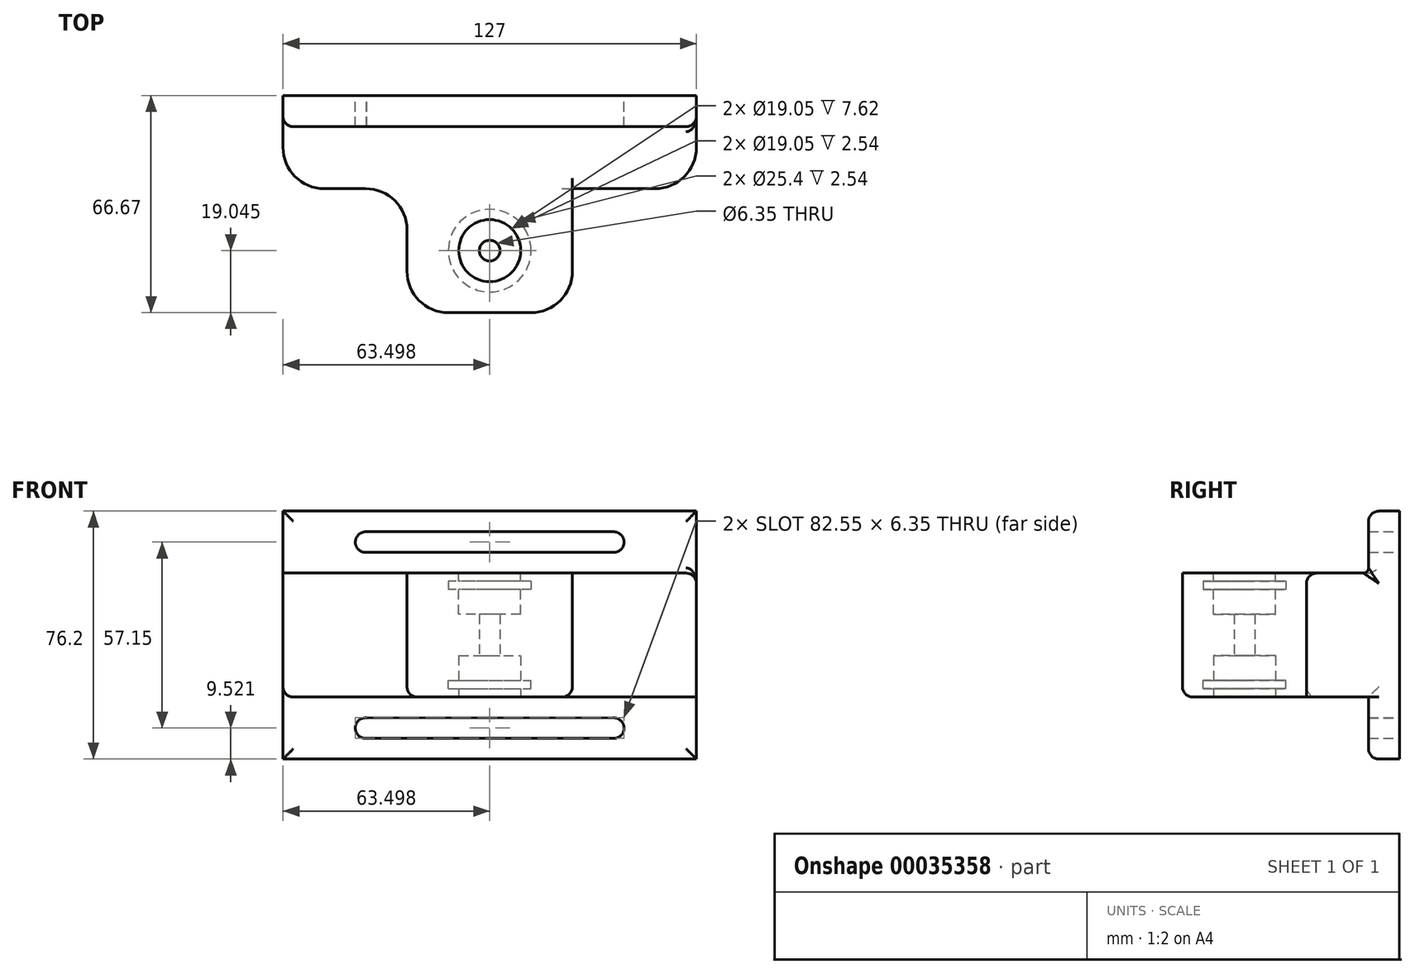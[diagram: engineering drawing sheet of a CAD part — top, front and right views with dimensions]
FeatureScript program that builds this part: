
annotation { "Feature Type Name" : "Feature", "Feature Type Description" : "" }
export const myFeature = defineFeature(function(context is Context, id is Id, definition is map)
    precondition{}
    {
        {
            var Q0;
            Q0=qCreatedBy(makeId("Front.planeOp"),FACE);
            var sketch = newSketch(context, id + "F0", { "sketchPlane" : qUnion([Q0])});
            skLineSegment(sketch, "E0.bottom", {"start": v(-70.41, 43.13) * mm, "end": v(56.59, 43.13) * mm});
            skLineSegment(sketch, "E0.top", {"start": v(-70.41, -33.07) * mm, "end": v(56.59, -33.07) * mm});
            skLineSegment(sketch, "E0.left", {"start": v(-70.41, 43.13) * mm, "end": v(-70.41, -33.07) * mm});
            skLineSegment(sketch, "E0.right", {"start": v(56.59, 43.13) * mm, "end": v(56.59, -33.07) * mm});
            skArc(sketch, "E1", {"start": v(-44.67, -20.4) * mm, "mid": v(-48.19, -23.48) * mm, "end": v(-44.8, -26.72) * mm});
            skArc(sketch, "E2", {"start": v(31.19, -26.72) * mm, "mid": v(34.36, -23.55) * mm, "end": v(31.19, -20.37) * mm});
            skLineSegment(sketch, "E3", {"start": v(-45.36, -20.4) * mm, "end": v(31.19, -20.37) * mm});
            skLineSegment(sketch, "E4", {"start": v(-45.23, -26.72) * mm, "end": v(31.19, -26.72) * mm});
            skLineSegment(sketch, "E5", {"start": v(-70.41, 5.03) * mm, "end": v(56.59, 5.03) * mm, "construction": true});
            skLineSegment(sketch, "E6.MirrorCS", {"start": v(-45.36, 30.44) * mm, "end": v(31.19, 30.43) * mm});
            skLineSegment(sketch, "E7.MirrorCS", {"start": v(-45.23, 36.77) * mm, "end": v(31.19, 36.78) * mm});
            skArc(sketch, "E8.MirrorCS", {"start": v(31.19, 36.78) * mm, "mid": v(34.36, 33.6) * mm, "end": v(31.19, 30.43) * mm});
            skArc(sketch, "E9.MirrorCS", {"start": v(-44.67, 30.44) * mm, "mid": v(-48.19, 33.53) * mm, "end": v(-44.8, 36.77) * mm});
            skSolve(sketch);
        }
        {
            var Q0;
            Q0=makeQuery(id+"F0.imprint","IMPRINT",FACE,{"disambiguationData":[TD([[makeQuery(id+"F0.imprint","IMPRINT",EDGE,{"derivedFrom":sQuery(id+"F0.wireOp",EDGE,"E0.bottom")}),-1.0]])]});
            extrude(context, id + "F1", {"entities" : qUnion([Q0]), "depth" : 9.52 * mm});
        }
        {
            var Q0;
            Q0=makeQuery(id+"F1.opExtrude","CAP_FACE",FACE,{"disambiguationData":[OSD([sQuery(id+"F0.wireOp",EDGE,"E0.bottom"),sQuery(id+"F0.wireOp",EDGE,"E0.top"),sQuery(id+"F0.wireOp",EDGE,"E0.left"),sQuery(id+"F0.wireOp",EDGE,"E0.right"),sQuery(id+"F0.wireOp",EDGE,"E1"),sQuery(id+"F0.wireOp",EDGE,"E2"),sQuery(id+"F0.wireOp",EDGE,"E3"),sQuery(id+"F0.wireOp",EDGE,"E4"),sQuery(id+"F0.wireOp",EDGE,"E6.MirrorCS"),sQuery(id+"F0.wireOp",EDGE,"E7.MirrorCS"),sQuery(id+"F0.wireOp",EDGE,"E8.MirrorCS"),sQuery(id+"F0.wireOp",EDGE,"E9.MirrorCS")])],"isStart":false});
            var sketch = newSketch(context, id + "F2", { "sketchPlane" : qUnion([Q0])});
            skLineSegment(sketch, "E10.bottom", {"start": v(-70.41, -14.02) * mm, "end": v(56.59, -14.02) * mm});
            skLineSegment(sketch, "E10.top", {"start": v(-70.41, 24.08) * mm, "end": v(56.59, 24.08) * mm});
            skLineSegment(sketch, "E10.left", {"start": v(-70.41, -14.02) * mm, "end": v(-70.41, 24.08) * mm});
            skLineSegment(sketch, "E10.right", {"start": v(56.59, -14.02) * mm, "end": v(56.59, 24.08) * mm});
            skSolve(sketch);
        }
        {
            var Q0;
            Q0=makeQuery(id+"F2.imprint","IMPRINT",FACE,{"disambiguationData":[TD([[makeQuery(id+"F2.imprint","IMPRINT",EDGE,{"derivedFrom":sQuery(id+"F2.wireOp",EDGE,"E10.bottom")}),1.0]])]});
            extrude(context, id + "F3", {"entities" : qUnion([Q0]), "operationType" : NewBodyOperationType.ADD, "depth" : 19.05 * mm});
        }
        {
            var Q0;
            Q0=makeQuery(id+"F3.opExtrude","CAP_FACE",FACE,{"disambiguationData":[OSD([sQuery(id+"F2.wireOp",EDGE,"E10.bottom"),sQuery(id+"F2.wireOp",EDGE,"E10.top"),sQuery(id+"F2.wireOp",EDGE,"E10.left"),sQuery(id+"F2.wireOp",EDGE,"E10.right")])],"isStart":false});
            var sketch = newSketch(context, id + "F4", { "sketchPlane" : qUnion([Q0])});
            skLineSegment(sketch, "E11.bottom", {"start": v(-32.31, -14.02) * mm, "end": v(18.49, -14.02) * mm});
            skLineSegment(sketch, "E11.top", {"start": v(-32.31, 24.08) * mm, "end": v(18.49, 24.08) * mm});
            skLineSegment(sketch, "E11.left", {"start": v(-32.31, -14.02) * mm, "end": v(-32.31, 24.08) * mm});
            skLineSegment(sketch, "E11.right", {"start": v(18.49, -14.02) * mm, "end": v(18.49, 24.08) * mm});
            skSolve(sketch);
        }
        {
            var Q0;
            Q0=makeQuery(id+"F4.imprint","IMPRINT",FACE,{"disambiguationData":[TD([[makeQuery(id+"F4.imprint","IMPRINT",EDGE,{"derivedFrom":sQuery(id+"F4.wireOp",EDGE,"E11.bottom")}),1.0]])]});
            extrude(context, id + "F5", {"entities" : qUnion([Q0]), "operationType" : NewBodyOperationType.ADD, "depth" : 38.1 * mm});
        }
        {
            var Q0;
            Q0=makeQuery(id+"F5.boolean.opBoolean","MERGE",FACE,{"derivedFrom":[makeQuery(id+"F3.opExtrude","SWEPT_FACE",FACE,{"disambiguationData":[OSD([sQuery(id+"F2.wireOp",EDGE,"E10.bottom")])]}),makeQuery(id+"F5.opExtrude","SWEPT_FACE",FACE,{"disambiguationData":[OSD([sQuery(id+"F4.wireOp",EDGE,"E11.bottom")])]})]});
            var sketch = newSketch(context, id + "F6", { "sketchPlane" : qUnion([Q0])});
            skPoint(sketch, "E12", {"position": v(-6.91, 47.63) * mm});
            skSolve(sketch);
        }
        {
            var Q0;
            Q0=sQuery(id+"F6.wireOp",VERTEX,"E12");
            var Q1;
            Q1=makeQuery(id+"F1.opExtrude","SWEPT_BODY",BODY,{"disambiguationData":[OSD([sQuery(id+"F0.wireOp",EDGE,"E0.bottom"),sQuery(id+"F0.wireOp",EDGE,"E0.top"),sQuery(id+"F0.wireOp",EDGE,"E0.left"),sQuery(id+"F0.wireOp",EDGE,"E0.right"),sQuery(id+"F0.wireOp",EDGE,"E1"),sQuery(id+"F0.wireOp",EDGE,"E2"),sQuery(id+"F0.wireOp",EDGE,"E3"),sQuery(id+"F0.wireOp",EDGE,"E4"),sQuery(id+"F0.wireOp",EDGE,"E6.MirrorCS"),sQuery(id+"F0.wireOp",EDGE,"E7.MirrorCS"),sQuery(id+"F0.wireOp",EDGE,"E8.MirrorCS"),sQuery(id+"F0.wireOp",EDGE,"E9.MirrorCS")])]});
            hole(context, id + "F7", {"style" : HoleStyle.C_BORE, "holeDiameter" : 6.35 * mm, "cBoreDiameter" : 19.05 * mm, "cBoreDepth" : 12.7 * mm, "endStyle" : HoleEndStyle.THROUGH, "locations" : qUnion([Q0]), "scope" : qUnion([Q1])});
        }
        {
            var Q0;
            Q0=makeQuery(id+"F5.boolean.opBoolean","MERGE",FACE,{"derivedFrom":[makeQuery(id+"F3.opExtrude","SWEPT_FACE",FACE,{"disambiguationData":[OSD([sQuery(id+"F2.wireOp",EDGE,"E10.top")])]}),makeQuery(id+"F5.opExtrude","SWEPT_FACE",FACE,{"disambiguationData":[OSD([sQuery(id+"F4.wireOp",EDGE,"E11.top")])]})]});
            var sketch = newSketch(context, id + "F8", { "sketchPlane" : qUnion([Q0])});
            skCircle(sketch, "E13.0.0", {"center": v(-6.91, -47.63) * mm, "radius": 9.52 * mm});
            skSolve(sketch);
        }
        {
            var Q0;
            Q0=makeQuery(id+"F8.imprint","IMPRINT",FACE,{"disambiguationData":[TD([[makeQuery(id+"F8.imprint","IMPRINT",EDGE,{"derivedFrom":sQuery(id+"F8.wireOp",EDGE,"E13.0.0")}),1.0]])]});
            extrude(context, id + "F9", {"entities" : qUnion([Q0]), "operationType" : NewBodyOperationType.REMOVE, "oppositeDirection" : true, "depth" : 12.7 * mm});
        }
        {
            var Q0;
            Q0=makeQuery(id+"F5.opExtrude","CAP_EDGE",EDGE,{"disambiguationData":[OSD([sQuery(id+"F4.wireOp",EDGE,"E11.right")])],"isStart":false});
            var Q1;
            Q1=makeQuery(id+"F5.opExtrude","CAP_EDGE",EDGE,{"disambiguationData":[OSD([sQuery(id+"F4.wireOp",EDGE,"E11.left")])],"isStart":false});
            var Q2;
            Q2=makeQuery(id+"F3.opExtrude","CAP_EDGE",EDGE,{"disambiguationData":[OSD([sQuery(id+"F2.wireOp",EDGE,"E10.left")])],"isStart":false});
            var Q3;
            Q3=makeQuery(id+"F5.opExtrude","CAP_EDGE",EDGE,{"disambiguationData":[OSD([sQuery(id+"F4.wireOp",EDGE,"E11.left")])],"isStart":true});
            var Q4;
            Q4=makeQuery(id+"F5.opExtrude","CAP_EDGE",EDGE,{"disambiguationData":[OSD([sQuery(id+"F4.wireOp",EDGE,"E11.right")])],"isStart":true});
            var Q5;
            Q5=makeQuery(id+"F3.opExtrude","CAP_EDGE",EDGE,{"disambiguationData":[OSD([sQuery(id+"F2.wireOp",EDGE,"E10.right")])],"isStart":false});
            fillet(context, id + "F10", {"entities" : qUnion([Q0, Q1, Q2, Q3, Q4, Q5]), "radius" : 12.7 * mm, "tangentPropagation" : true, "allowEdgeOverflow" : false});
        }
        {
            var Q0;
            Q0=makeQuery(id+"F1.opExtrude","SWEPT_FACE",FACE,{"disambiguationData":[OSD([sQuery(id+"F0.wireOp",EDGE,"E0.top")])]});
            cPlane(context, id + "F11", {"entities" : qUnion([Q0]), "cplaneType" : CPlaneType.OFFSET, "offset" : 24.13 * mm, "oppositeDirection" : true, "width" : 152.4 * mm, "height" : 152.4 * mm});
        }
        {
            var Q0;
            Q0=qCreatedBy(id+"F11.planeOp",FACE);
            var sketch = newSketch(context, id + "F12", { "sketchPlane" : qUnion([Q0])});
            skCircle(sketch, "E14", {"center": v(-6.91, 47.63) * mm, "radius": 12.7 * mm});
            skSolve(sketch);
        }
        {
            var Q0;
            Q0=makeQuery(id+"F1.opExtrude","SWEPT_FACE",FACE,{"disambiguationData":[OSD([sQuery(id+"F0.wireOp",EDGE,"E0.bottom")])]});
            cPlane(context, id + "F13", {"entities" : qUnion([Q0]), "cplaneType" : CPlaneType.OFFSET, "offset" : 24.13 * mm, "oppositeDirection" : true, "width" : 152.4 * mm, "height" : 152.4 * mm});
        }
        {
            var Q0;
            Q0=qCreatedBy(id+"F13.planeOp",FACE);
            var sketch = newSketch(context, id + "F14", { "sketchPlane" : qUnion([Q0])});
            skCircle(sketch, "E15.0", {"center": v(-6.91, -47.63) * mm, "radius": 12.7 * mm});
            skSolve(sketch);
        }
        {
            var Q0;
            Q0 = qSketchRegion(id + "F14", true);
            var Q1;
            Q1=makeQuery(id+"F5.boolean.opBoolean","MERGE",FACE,{"derivedFrom":[makeQuery(id+"F3.opExtrude","SWEPT_FACE",FACE,{"disambiguationData":[OSD([sQuery(id+"F2.wireOp",EDGE,"E10.top")])]}),makeQuery(id+"F5.opExtrude","SWEPT_FACE",FACE,{"disambiguationData":[OSD([sQuery(id+"F4.wireOp",EDGE,"E11.top")])]})]});
            extrude(context, id + "F15", {"entities" : qUnion([Q0, Q1]), "operationType" : NewBodyOperationType.REMOVE, "depth" : 2.54 * mm});
        }
        {
            var Q0;
            Q0 = qSketchRegion(id + "F12", true);
            var Q1;
            Q1=makeQuery(id+"F5.boolean.opBoolean","MERGE",FACE,{"derivedFrom":[makeQuery(id+"F3.opExtrude","SWEPT_FACE",FACE,{"disambiguationData":[OSD([sQuery(id+"F2.wireOp",EDGE,"E10.bottom")])]}),makeQuery(id+"F5.opExtrude","SWEPT_FACE",FACE,{"disambiguationData":[OSD([sQuery(id+"F4.wireOp",EDGE,"E11.bottom")])]})]});
            extrude(context, id + "F16", {"entities" : qUnion([Q0, Q1]), "operationType" : NewBodyOperationType.REMOVE, "depth" : 2.54 * mm});
        }
        {
            var Q0;
            Q0=makeQuery(id+"F10.opFillet","BLEND_EDGE",EDGE,{"blendedFrom":[makeQuery(id+"F3.opExtrude","CAP_EDGE",EDGE,{"disambiguationData":[OSD([sQuery(id+"F2.wireOp",EDGE,"E10.left")])],"isStart":false}),makeQuery(id+"F5.boolean.opBoolean","MERGE",FACE,{"derivedFrom":[makeQuery(id+"F3.opExtrude","SWEPT_FACE",FACE,{"disambiguationData":[OSD([sQuery(id+"F2.wireOp",EDGE,"E10.bottom")])]}),makeQuery(id+"F5.opExtrude","SWEPT_FACE",FACE,{"disambiguationData":[OSD([sQuery(id+"F4.wireOp",EDGE,"E11.bottom")])]})]})],"blendedInto":[makeQuery(id+"F5.boolean.opBoolean","MERGE",FACE,{"derivedFrom":[makeQuery(id+"F3.opExtrude","SWEPT_FACE",FACE,{"disambiguationData":[OSD([sQuery(id+"F2.wireOp",EDGE,"E10.bottom")])]}),makeQuery(id+"F5.opExtrude","SWEPT_FACE",FACE,{"disambiguationData":[OSD([sQuery(id+"F4.wireOp",EDGE,"E11.bottom")])]})]})]});
            var Q1;
            Q1=makeQuery(id+"F10.opFillet","BLEND_EDGE",EDGE,{"blendedFrom":[makeQuery(id+"F3.opExtrude","CAP_EDGE",EDGE,{"disambiguationData":[OSD([sQuery(id+"F2.wireOp",EDGE,"E10.right")])],"isStart":false}),makeQuery(id+"F5.boolean.opBoolean","MERGE",FACE,{"derivedFrom":[makeQuery(id+"F3.opExtrude","SWEPT_FACE",FACE,{"disambiguationData":[OSD([sQuery(id+"F2.wireOp",EDGE,"E10.top")])]}),makeQuery(id+"F5.opExtrude","SWEPT_FACE",FACE,{"disambiguationData":[OSD([sQuery(id+"F4.wireOp",EDGE,"E11.top")])]})]})],"blendedInto":[makeQuery(id+"F5.boolean.opBoolean","MERGE",FACE,{"derivedFrom":[makeQuery(id+"F3.opExtrude","SWEPT_FACE",FACE,{"disambiguationData":[OSD([sQuery(id+"F2.wireOp",EDGE,"E10.top")])]}),makeQuery(id+"F5.opExtrude","SWEPT_FACE",FACE,{"disambiguationData":[OSD([sQuery(id+"F4.wireOp",EDGE,"E11.top")])]})]})]});
            var Q2;
            {var subQ0=sQuery(id+"F0.wireOp",EDGE,"E0.right");var subQ1=sQuery(id+"F0.wireOp",EDGE,"E0.bottom");Q2=makeQuery(id+"F3.boolean.opBoolean","SPLIT",EDGE,{"disambiguationData":[TD([makeQuery(id+"F1.opExtrude","SWEPT_FACE",FACE,{"disambiguationData":[OSD([subQ1])]})])],"derivedFrom":makeQuery(id+"F1.opExtrude","CAP_EDGE",EDGE,{"disambiguationData":[OSD([subQ0])],"isStart":false})});}
            var Q3;
            Q3=makeQuery(id+"F1.opExtrude","CAP_EDGE",EDGE,{"disambiguationData":[OSD([sQuery(id+"F0.wireOp",EDGE,"E0.bottom")])],"isStart":false});
            var Q4;
            {var subQ0=sQuery(id+"F0.wireOp",EDGE,"E0.left");var subQ1=sQuery(id+"F0.wireOp",EDGE,"E0.bottom");Q4=makeQuery(id+"F3.boolean.opBoolean","SPLIT",EDGE,{"disambiguationData":[TD([makeQuery(id+"F1.opExtrude","SWEPT_FACE",FACE,{"disambiguationData":[OSD([subQ1])]})])],"derivedFrom":makeQuery(id+"F1.opExtrude","CAP_EDGE",EDGE,{"disambiguationData":[OSD([subQ0])],"isStart":false})});}
            var Q5;
            {var subQ0=sQuery(id+"F0.wireOp",EDGE,"E0.left");var subQ1=sQuery(id+"F0.wireOp",EDGE,"E0.top");Q5=makeQuery(id+"F3.boolean.opBoolean","SPLIT",EDGE,{"disambiguationData":[TD([makeQuery(id+"F1.opExtrude","SWEPT_FACE",FACE,{"disambiguationData":[OSD([subQ1])]})])],"derivedFrom":makeQuery(id+"F1.opExtrude","CAP_EDGE",EDGE,{"disambiguationData":[OSD([subQ0])],"isStart":false})});}
            var Q6;
            Q6=makeQuery(id+"F1.opExtrude","CAP_EDGE",EDGE,{"disambiguationData":[OSD([sQuery(id+"F0.wireOp",EDGE,"E0.top")])],"isStart":false});
            var Q7;
            {var subQ0=sQuery(id+"F0.wireOp",EDGE,"E0.right");var subQ1=sQuery(id+"F0.wireOp",EDGE,"E0.top");Q7=makeQuery(id+"F3.boolean.opBoolean","SPLIT",EDGE,{"disambiguationData":[TD([makeQuery(id+"F1.opExtrude","SWEPT_FACE",FACE,{"disambiguationData":[OSD([subQ1])]})])],"derivedFrom":makeQuery(id+"F1.opExtrude","CAP_EDGE",EDGE,{"disambiguationData":[OSD([subQ0])],"isStart":false})});}
            fillet(context, id + "F17", {"entities" : qUnion([Q0, Q1, Q2, Q3, Q4, Q5, Q6, Q7]), "radius" : 3.17 * mm, "tangentPropagation" : true, "allowEdgeOverflow" : false});
        }
        {
            var Q0;
            Q0=makeQuery(id+"F3.opExtrude","CAP_EDGE",EDGE,{"disambiguationData":[OSD([sQuery(id+"F2.wireOp",EDGE,"E10.bottom")])],"isStart":true});
            var Q1;
            Q1=makeQuery(id+"F3.opExtrude","CAP_EDGE",EDGE,{"disambiguationData":[OSD([sQuery(id+"F2.wireOp",EDGE,"E10.top")])],"isStart":true});
            fillet(context, id + "F18", {"entities" : qUnion([Q0, Q1]), "radius" : 1.59 * mm, "tangentPropagation" : true, "allowEdgeOverflow" : false});
        }
    });
